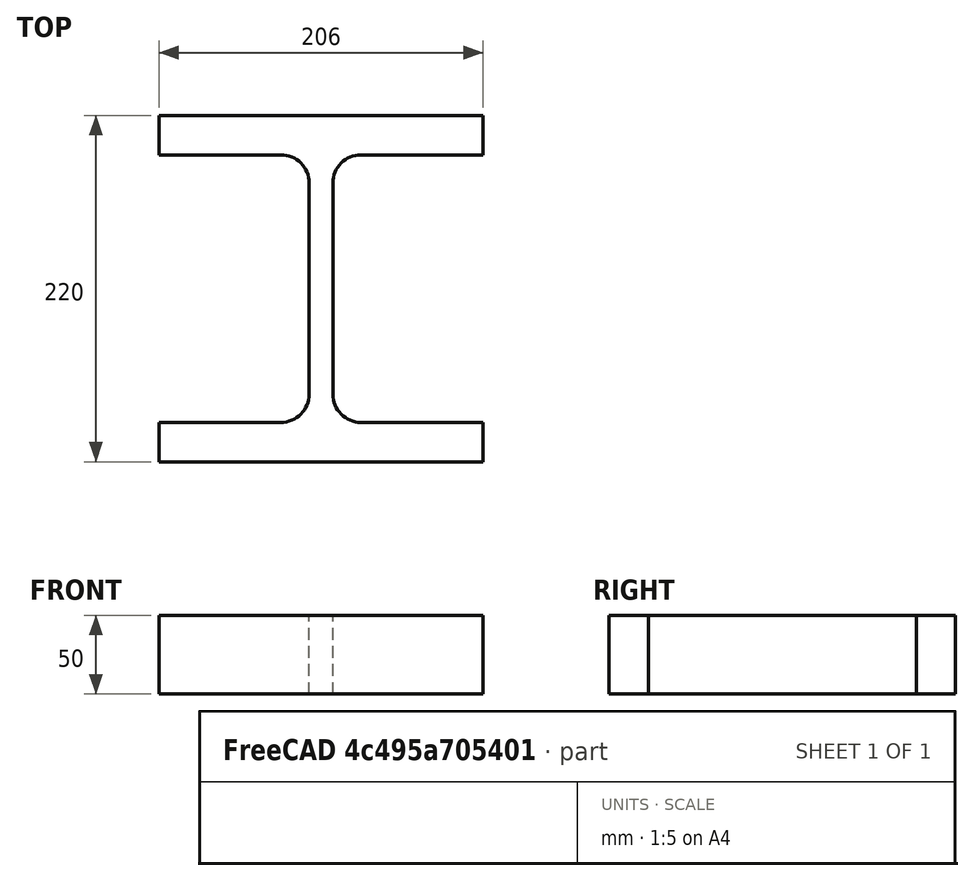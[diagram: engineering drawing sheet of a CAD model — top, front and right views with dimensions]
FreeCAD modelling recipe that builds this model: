
FCSTD DOCUMENT  (FreeCAD 0.15R4671 (Git))
Label: HE-M-Profile 200 DIN1025-4 S235JR
License: All rights reserved
LicenseURL: http://en.wikipedia.org/wiki/All_rights_reserved
objects: Sketcher::SketchObject×1, Part::Extrusion×1
note: 2 computed .brp shape members not serialized (recipe doc carries the construction recipe); baked Part::Feature solids carry a one-line shape summary decoded from their .brp

FEATURE [Sketcher::SketchObject] Sketch
  sketch-geometry (16):
    g0: LineSegment StartX=7.5 StartY=-67 StartZ=0 EndX=7.5 EndY=67 EndZ=0
    g1: LineSegment StartX=25.5 StartY=85 StartZ=0 EndX=103 EndY=85 EndZ=0
    g2: LineSegment StartX=103 StartY=85 StartZ=0 EndX=103 EndY=110 EndZ=0
    g3: LineSegment StartX=103 StartY=110 StartZ=0 EndX=-103 EndY=110 EndZ=0
    g4: LineSegment StartX=-103 StartY=110 StartZ=0 EndX=-103 EndY=85 EndZ=0
    g5: LineSegment StartX=-103 StartY=85 StartZ=0 EndX=-25.5 EndY=85 EndZ=0
    g6: LineSegment StartX=-7.5 StartY=67 StartZ=0 EndX=-7.5 EndY=-67 EndZ=0
    g7: LineSegment StartX=-25.5 StartY=-85 StartZ=0 EndX=-103 EndY=-85 EndZ=0
    g8: LineSegment StartX=-103 StartY=-85 StartZ=0 EndX=-103 EndY=-110 EndZ=0
    g9: LineSegment StartX=-103 StartY=-110 StartZ=0 EndX=103 EndY=-110 EndZ=0
    g10: LineSegment StartX=103 StartY=-110 StartZ=0 EndX=103 EndY=-85 EndZ=0
    g11: LineSegment StartX=103 StartY=-85 StartZ=0 EndX=25.5 EndY=-85 EndZ=0
    g12: ArcOfCircle CenterX=25.5 CenterY=67 CenterZ=0 NormalX=0 NormalY=0 NormalZ=1 Radius=18 StartAngle=1.5708 EndAngle=3.14159
    g13: ArcOfCircle CenterX=25.5 CenterY=-67 CenterZ=0 NormalX=0 NormalY=0 NormalZ=1 Radius=18 StartAngle=3.14159 EndAngle=4.71239
    g14: ArcOfCircle CenterX=-25.5 CenterY=67 CenterZ=0 NormalX=0 NormalY=0 NormalZ=1 Radius=18 StartAngle=0 EndAngle=1.5708
    g15: ArcOfCircle CenterX=-25.5 CenterY=-67 CenterZ=0 NormalX=0 NormalY=0 NormalZ=1 Radius=18 StartAngle=4.71239 EndAngle=6.28319
  constraints (42):
    c: Vertical(g0)
    c: Coincident(g2,g1)
    c: Vertical(g2)
    c: Coincident(g3,g2)
    c: Coincident(g4,g3)
    c: Vertical(g4)
    c: Coincident(g5,g4)
    c: Horizontal(g5)
    c: Vertical(g6)
    c: Horizontal(g7)
    c: Coincident(g8,g7)
    c: Vertical(g8)
    c: Coincident(g9,g8)
    c: Horizontal(g9)
    c: Coincident(g10,g9)
    c: Vertical(g10)
    c: Coincident(g11,g10)
    c: Horizontal(g11)
    c: Tangent(g1,g12) = 1.5708
    c: Tangent(g0,g12) = 1.5708
    c: Tangent(g0,g13) = 1.5708
    c: Tangent(g11,g13) = 1.5708
    c: Tangent(g5,g14) = 1.5708
    c: Tangent(g6,g14) = 1.5708
    c: Tangent(g6,g15) = 1.5708
    c: Tangent(g7,g15) = 1.5708
    c: Equal(g3,g9)
    c: Equal(g2,g4)
    c: Equal(g4,g8)
    c: Equal(g8,g10)
    c: Equal(g12,g14)
    c: Equal(g14,g15)
    c: Equal(g15,g13)
    c: Symmetric(g2,g3,g-2)
    c: Symmetric(g9,g8,g-2)
    c: Symmetric(g0,g6,g-2)
    c: Symmetric(g2,g9,g-1)
    c: DistanceY(g2,g9) = -220
    c: DistanceX(g3) = -206
    c: DistanceX(g0,g6) = -15
    c: DistanceY(g2) = 25
    c: Radius(g12) = 18
FEATURE [Part::Extrusion] Extrude  label="HE-M-Profile 200 DIN1025-4 S235JR"
  Base = -> Sketch
  Dir = (0,0,50)
  Solid = true
